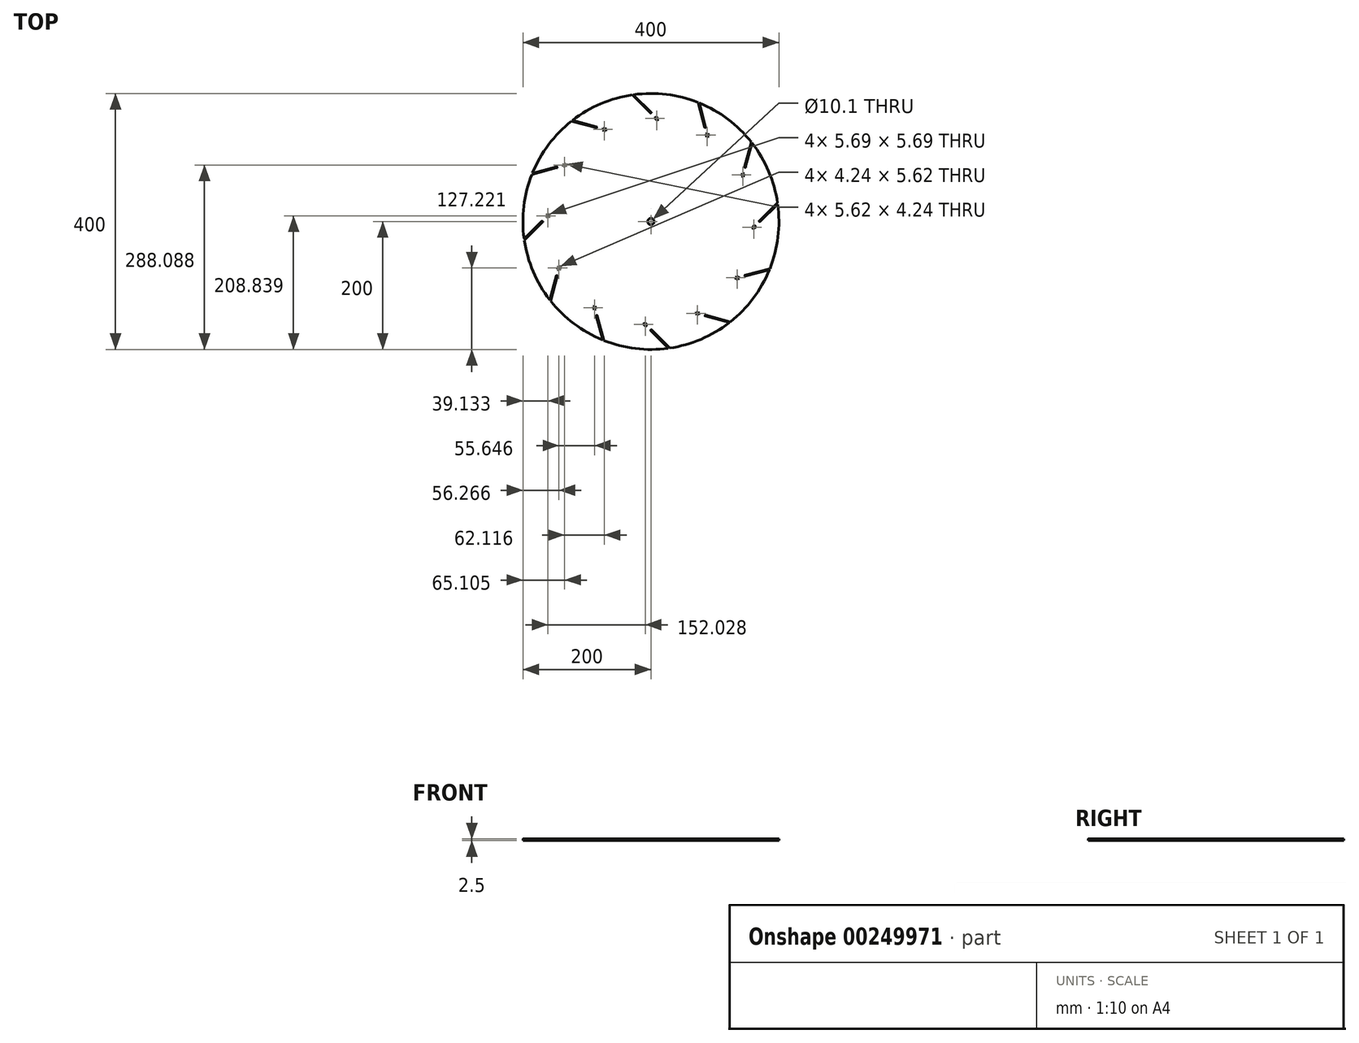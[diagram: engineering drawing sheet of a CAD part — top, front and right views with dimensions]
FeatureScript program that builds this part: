
annotation { "Feature Type Name" : "Feature", "Feature Type Description" : "" }
export const myFeature = defineFeature(function(context is Context, id is Id, definition is map)
    precondition{}
    {
        {
            var Q0;
            Q0=qCreatedBy(makeId("Top.planeOp"),FACE);
            var sketch = newSketch(context, id + "F0", { "sketchPlane" : qUnion([Q0])});
            skArc(sketch, "E0", {"start": v(-197.85, -29.24) * mm, "mid": v(-184.02, -78.33) * mm, "end": v(-158.23, -122.33) * mm});
            skLineSegment(sketch, "E1", {"start": v(28.28, 28.28) * mm, "end": v(-28.28, -28.28) * mm, "construction": true});
            skCircle(sketch, "E2", {"center": v(0, 0) * mm, "radius": 40 * mm, "construction": true});
            skLineSegment(sketch, "E3", {"start": v(40, 0) * mm, "end": v(-286.23, 0) * mm, "construction": true});
            skLineSegment(sketch, "E4", {"start": v(-28.28, -28.28) * mm, "end": v(-235.32, -28.28) * mm, "construction": true});
            skLineSegment(sketch, "E5", {"start": v(-197.99, -28.28) * mm, "end": v(-113.58, 56.13) * mm, "construction": true});
            skPoint(sketch, "E6", {"position": v(-169.7, 0) * mm});
            skCircle(sketch, "E7", {"center": v(0, 0) * mm, "radius": 169.7 * mm, "construction": true});
            skCircle(sketch, "E8", {"center": v(-169.7, 0) * mm, "radius": 0.78 * mm, "construction": true});
            skPoint(sketch, "E9", {"position": v(-197.99, -28.28) * mm});
            skLineSegment(sketch, "E10", {"start": v(-197.44, -28.83) * mm, "end": v(-198.54, -27.74) * mm, "construction": true});
            skCircle(sketch, "E11", {"center": v(-169.7, 0) * mm, "radius": 40 * mm, "construction": true});
            skLineSegment(sketch, "E12.trimOffspring", {"start": v(-170.36, 0.44) * mm, "end": v(-197.62, -26.82) * mm});
            skLineSegment(sketch, "E13.trimOffspring", {"start": v(-169.26, -0.65) * mm, "end": v(-197.85, -29.24) * mm});
            skLineSegment(sketch, "E14", {"start": v(-170.15, 0.44) * mm, "end": v(-169.26, -0.44) * mm});
            skLineSegment(sketch, "E15.MirrorCS", {"start": v(-170.25, 0.55) * mm, "end": v(-141.97, 28.83) * mm, "construction": true});
            skLineSegment(sketch, "E16.MirrorCS", {"start": v(-169.16, -0.55) * mm, "end": v(-140.87, 27.74) * mm, "construction": true});
            skLineSegment(sketch, "E17.MirrorCS", {"start": v(-140.87, 27.74) * mm, "end": v(-141.97, 28.83) * mm, "construction": true});
            skLineSegment(sketch, "E18", {"start": v(-163.71, 8.15) * mm, "end": v(-161.56, 6) * mm});
            skLineSegment(sketch, "E19", {"start": v(-160.18, 11.68) * mm, "end": v(-158.02, 9.53) * mm});
            skLineSegment(sketch, "E20.trimOffspring", {"start": v(-161.56, 6) * mm, "end": v(-158.02, 9.53) * mm});
            skLineSegment(sketch, "E21.trimOffspring", {"start": v(-163.71, 8.15) * mm, "end": v(-160.18, 11.68) * mm});
            skLineSegment(sketch, "E22.trimOffspring", {"start": v(-198.53, -27.73) * mm, "end": v(-198.54, -27.74) * mm});
            skCircle(sketch, "E23", {"center": v(0, 0) * mm, "radius": 5.05 * mm});
            skArc(sketch, "E24", {"start": v(-170.15, 0.44) * mm, "mid": v(-170.25, 0.7) * mm, "end": v(-170.36, 0.44) * mm});
            skArc(sketch, "E25.MirrorC", {"start": v(-169.26, -0.44) * mm, "mid": v(-169, -0.55) * mm, "end": v(-169.26, -0.65) * mm});
            skPoint(sketch, "E26.orphan", {"position": v(-198.12, -27.32) * mm});
            skLineSegment(sketch, "E27.trimOffspring", {"start": v(-197.62, -26.82) * mm, "end": v(-198.2, -26.82) * mm});
            skLineSegment(sketch, "E28.1.0", {"start": v(-184.56, 75.58) * mm, "end": v(-185.05, 75.87) * mm});
            skLineSegment(sketch, "E28.1.1", {"start": v(-147.31, 85.56) * mm, "end": v(-184.56, 75.58) * mm});
            skArc(sketch, "E28.1.2", {"start": v(-147.13, 85.46) * mm, "mid": v(-147.1, 85.73) * mm, "end": v(-147.31, 85.56) * mm});
            skLineSegment(sketch, "E28.1.3", {"start": v(-147.13, 85.46) * mm, "end": v(-146.8, 84.25) * mm});
            skArc(sketch, "E28.1.4", {"start": v(-146.8, 84.25) * mm, "mid": v(-146.64, 84.03) * mm, "end": v(-146.91, 84.07) * mm});
            skLineSegment(sketch, "E28.1.5", {"start": v(-146.91, 84.07) * mm, "end": v(-185.96, 73.6) * mm});
            skLineSegment(sketch, "E28.1.6", {"start": v(-137.7, 88.91) * mm, "end": v(-132.88, 90.2) * mm});
            skLineSegment(sketch, "E28.1.7", {"start": v(-132.88, 90.2) * mm, "end": v(-132.09, 87.26) * mm});
            skLineSegment(sketch, "E28.1.8", {"start": v(-136.92, 85.97) * mm, "end": v(-132.09, 87.26) * mm});
            skLineSegment(sketch, "E28.1.9", {"start": v(-137.7, 88.91) * mm, "end": v(-136.92, 85.97) * mm});
            skLineSegment(sketch, "E28.2.0", {"start": v(-122.04, 157.74) * mm, "end": v(-122.33, 158.23) * mm});
            skLineSegment(sketch, "E28.2.1", {"start": v(-84.8, 147.76) * mm, "end": v(-122.04, 157.74) * mm});
            skArc(sketch, "E28.2.2", {"start": v(-84.7, 147.57) * mm, "mid": v(-84.52, 147.8) * mm, "end": v(-84.8, 147.76) * mm});
            skLineSegment(sketch, "E28.2.3", {"start": v(-84.7, 147.57) * mm, "end": v(-85.01, 146.37) * mm});
            skArc(sketch, "E28.2.4", {"start": v(-85.01, 146.37) * mm, "mid": v(-84.98, 146.1) * mm, "end": v(-85.2, 146.26) * mm});
            skLineSegment(sketch, "E28.2.5", {"start": v(-85.2, 146.26) * mm, "end": v(-124.25, 156.72) * mm});
            skLineSegment(sketch, "E28.2.6", {"start": v(-74.8, 145.85) * mm, "end": v(-69.97, 144.56) * mm});
            skLineSegment(sketch, "E28.2.7", {"start": v(-69.97, 144.56) * mm, "end": v(-70.76, 141.61) * mm});
            skLineSegment(sketch, "E28.2.8", {"start": v(-75.59, 142.9) * mm, "end": v(-70.76, 141.61) * mm});
            skLineSegment(sketch, "E28.2.9", {"start": v(-74.8, 145.85) * mm, "end": v(-75.59, 142.9) * mm});
            skLineSegment(sketch, "E28.3.0", {"start": v(-26.82, 197.62) * mm, "end": v(-26.82, 198.2) * mm});
            skLineSegment(sketch, "E28.3.1", {"start": v(0.44, 170.36) * mm, "end": v(-26.82, 197.62) * mm});
            skArc(sketch, "E28.3.2", {"start": v(0.44, 170.15) * mm, "mid": v(0.7, 170.25) * mm, "end": v(0.44, 170.36) * mm});
            skLineSegment(sketch, "E28.3.3", {"start": v(0.44, 170.15) * mm, "end": v(-0.44, 169.26) * mm});
            skArc(sketch, "E28.3.4", {"start": v(-0.44, 169.26) * mm, "mid": v(-0.55, 169) * mm, "end": v(-0.65, 169.26) * mm});
            skLineSegment(sketch, "E28.3.5", {"start": v(-0.65, 169.26) * mm, "end": v(-29.24, 197.85) * mm});
            skLineSegment(sketch, "E28.3.6", {"start": v(8.15, 163.71) * mm, "end": v(11.68, 160.18) * mm});
            skLineSegment(sketch, "E28.3.7", {"start": v(11.68, 160.18) * mm, "end": v(9.53, 158.02) * mm});
            skLineSegment(sketch, "E28.3.8", {"start": v(6, 161.56) * mm, "end": v(9.53, 158.02) * mm});
            skLineSegment(sketch, "E28.3.9", {"start": v(8.15, 163.71) * mm, "end": v(6, 161.56) * mm});
            skLineSegment(sketch, "E28.4.0", {"start": v(75.58, 184.56) * mm, "end": v(75.87, 185.05) * mm});
            skLineSegment(sketch, "E28.4.1", {"start": v(85.56, 147.31) * mm, "end": v(75.58, 184.56) * mm});
            skArc(sketch, "E28.4.2", {"start": v(85.46, 147.13) * mm, "mid": v(85.73, 147.1) * mm, "end": v(85.56, 147.31) * mm});
            skLineSegment(sketch, "E28.4.3", {"start": v(85.46, 147.13) * mm, "end": v(84.25, 146.8) * mm});
            skArc(sketch, "E28.4.4", {"start": v(84.25, 146.8) * mm, "mid": v(84.03, 146.64) * mm, "end": v(84.07, 146.91) * mm});
            skLineSegment(sketch, "E28.4.5", {"start": v(84.07, 146.91) * mm, "end": v(73.6, 185.96) * mm});
            skLineSegment(sketch, "E28.4.6", {"start": v(88.91, 137.7) * mm, "end": v(90.2, 132.88) * mm});
            skLineSegment(sketch, "E28.4.7", {"start": v(90.2, 132.88) * mm, "end": v(87.26, 132.09) * mm});
            skLineSegment(sketch, "E28.4.8", {"start": v(85.97, 136.92) * mm, "end": v(87.26, 132.09) * mm});
            skLineSegment(sketch, "E28.4.9", {"start": v(88.91, 137.7) * mm, "end": v(85.97, 136.92) * mm});
            skLineSegment(sketch, "E28.5.0", {"start": v(157.74, 122.04) * mm, "end": v(158.23, 122.33) * mm});
            skLineSegment(sketch, "E28.5.1", {"start": v(147.76, 84.8) * mm, "end": v(157.74, 122.04) * mm});
            skArc(sketch, "E28.5.2", {"start": v(147.57, 84.7) * mm, "mid": v(147.8, 84.52) * mm, "end": v(147.76, 84.8) * mm});
            skLineSegment(sketch, "E28.5.3", {"start": v(147.57, 84.7) * mm, "end": v(146.37, 85.01) * mm});
            skArc(sketch, "E28.5.4", {"start": v(146.37, 85.01) * mm, "mid": v(146.1, 84.98) * mm, "end": v(146.26, 85.2) * mm});
            skLineSegment(sketch, "E28.5.5", {"start": v(146.26, 85.2) * mm, "end": v(156.72, 124.25) * mm});
            skLineSegment(sketch, "E28.5.6", {"start": v(145.85, 74.8) * mm, "end": v(144.56, 69.97) * mm});
            skLineSegment(sketch, "E28.5.7", {"start": v(144.56, 69.97) * mm, "end": v(141.61, 70.76) * mm});
            skLineSegment(sketch, "E28.5.8", {"start": v(142.9, 75.59) * mm, "end": v(141.61, 70.76) * mm});
            skLineSegment(sketch, "E28.5.9", {"start": v(145.85, 74.8) * mm, "end": v(142.9, 75.59) * mm});
            skLineSegment(sketch, "E28.6.0", {"start": v(197.62, 26.82) * mm, "end": v(198.2, 26.82) * mm});
            skLineSegment(sketch, "E28.6.1", {"start": v(170.36, -0.44) * mm, "end": v(197.62, 26.82) * mm});
            skArc(sketch, "E28.6.2", {"start": v(170.15, -0.44) * mm, "mid": v(170.25, -0.7) * mm, "end": v(170.36, -0.44) * mm});
            skLineSegment(sketch, "E28.6.3", {"start": v(170.15, -0.44) * mm, "end": v(169.26, 0.44) * mm});
            skArc(sketch, "E28.6.4", {"start": v(169.26, 0.44) * mm, "mid": v(169, 0.55) * mm, "end": v(169.26, 0.65) * mm});
            skLineSegment(sketch, "E28.6.5", {"start": v(169.26, 0.65) * mm, "end": v(197.85, 29.24) * mm});
            skLineSegment(sketch, "E28.6.6", {"start": v(163.71, -8.15) * mm, "end": v(160.18, -11.68) * mm});
            skLineSegment(sketch, "E28.6.7", {"start": v(160.18, -11.68) * mm, "end": v(158.02, -9.53) * mm});
            skLineSegment(sketch, "E28.6.8", {"start": v(161.56, -6) * mm, "end": v(158.02, -9.53) * mm});
            skLineSegment(sketch, "E28.6.9", {"start": v(163.71, -8.15) * mm, "end": v(161.56, -6) * mm});
            skLineSegment(sketch, "E28.7.0", {"start": v(184.56, -75.58) * mm, "end": v(185.05, -75.87) * mm});
            skLineSegment(sketch, "E28.7.1", {"start": v(147.31, -85.56) * mm, "end": v(184.56, -75.58) * mm});
            skArc(sketch, "E28.7.2", {"start": v(147.13, -85.46) * mm, "mid": v(147.1, -85.73) * mm, "end": v(147.31, -85.56) * mm});
            skLineSegment(sketch, "E28.7.3", {"start": v(147.13, -85.46) * mm, "end": v(146.8, -84.25) * mm});
            skArc(sketch, "E28.7.4", {"start": v(146.8, -84.25) * mm, "mid": v(146.64, -84.03) * mm, "end": v(146.91, -84.07) * mm});
            skLineSegment(sketch, "E28.7.5", {"start": v(146.91, -84.07) * mm, "end": v(185.96, -73.6) * mm});
            skLineSegment(sketch, "E28.7.6", {"start": v(137.7, -88.91) * mm, "end": v(132.88, -90.2) * mm});
            skLineSegment(sketch, "E28.7.7", {"start": v(132.88, -90.2) * mm, "end": v(132.09, -87.26) * mm});
            skLineSegment(sketch, "E28.7.8", {"start": v(136.92, -85.97) * mm, "end": v(132.09, -87.26) * mm});
            skLineSegment(sketch, "E28.7.9", {"start": v(137.7, -88.91) * mm, "end": v(136.92, -85.97) * mm});
            skLineSegment(sketch, "E28.8.0", {"start": v(122.04, -157.74) * mm, "end": v(122.33, -158.23) * mm});
            skLineSegment(sketch, "E28.8.1", {"start": v(84.8, -147.76) * mm, "end": v(122.04, -157.74) * mm});
            skArc(sketch, "E28.8.2", {"start": v(84.7, -147.57) * mm, "mid": v(84.52, -147.8) * mm, "end": v(84.8, -147.76) * mm});
            skLineSegment(sketch, "E28.8.3", {"start": v(84.7, -147.57) * mm, "end": v(85.01, -146.37) * mm});
            skArc(sketch, "E28.8.4", {"start": v(85.01, -146.37) * mm, "mid": v(84.98, -146.1) * mm, "end": v(85.2, -146.26) * mm});
            skLineSegment(sketch, "E28.8.5", {"start": v(85.2, -146.26) * mm, "end": v(124.25, -156.72) * mm});
            skLineSegment(sketch, "E28.8.6", {"start": v(74.8, -145.85) * mm, "end": v(69.97, -144.56) * mm});
            skLineSegment(sketch, "E28.8.7", {"start": v(69.97, -144.56) * mm, "end": v(70.76, -141.61) * mm});
            skLineSegment(sketch, "E28.8.8", {"start": v(75.59, -142.9) * mm, "end": v(70.76, -141.61) * mm});
            skLineSegment(sketch, "E28.8.9", {"start": v(74.8, -145.85) * mm, "end": v(75.59, -142.9) * mm});
            skLineSegment(sketch, "E28.9.0", {"start": v(26.82, -197.62) * mm, "end": v(26.82, -198.2) * mm});
            skLineSegment(sketch, "E28.9.1", {"start": v(-0.44, -170.36) * mm, "end": v(26.82, -197.62) * mm});
            skArc(sketch, "E28.9.2", {"start": v(-0.44, -170.15) * mm, "mid": v(-0.7, -170.25) * mm, "end": v(-0.44, -170.36) * mm});
            skLineSegment(sketch, "E28.9.3", {"start": v(-0.44, -170.15) * mm, "end": v(0.44, -169.26) * mm});
            skArc(sketch, "E28.9.4", {"start": v(0.44, -169.26) * mm, "mid": v(0.55, -169) * mm, "end": v(0.65, -169.26) * mm});
            skLineSegment(sketch, "E28.9.5", {"start": v(0.65, -169.26) * mm, "end": v(29.24, -197.85) * mm});
            skLineSegment(sketch, "E28.9.6", {"start": v(-8.15, -163.71) * mm, "end": v(-11.68, -160.18) * mm});
            skLineSegment(sketch, "E28.9.7", {"start": v(-11.68, -160.18) * mm, "end": v(-9.53, -158.02) * mm});
            skLineSegment(sketch, "E28.9.8", {"start": v(-6, -161.56) * mm, "end": v(-9.53, -158.02) * mm});
            skLineSegment(sketch, "E28.9.9", {"start": v(-8.15, -163.71) * mm, "end": v(-6, -161.56) * mm});
            skLineSegment(sketch, "E28.10.0", {"start": v(-75.58, -184.56) * mm, "end": v(-75.87, -185.05) * mm});
            skLineSegment(sketch, "E28.10.1", {"start": v(-85.56, -147.31) * mm, "end": v(-75.58, -184.56) * mm});
            skArc(sketch, "E28.10.2", {"start": v(-85.46, -147.13) * mm, "mid": v(-85.73, -147.1) * mm, "end": v(-85.56, -147.31) * mm});
            skLineSegment(sketch, "E28.10.3", {"start": v(-85.46, -147.13) * mm, "end": v(-84.25, -146.8) * mm});
            skArc(sketch, "E28.10.4", {"start": v(-84.25, -146.8) * mm, "mid": v(-84.03, -146.64) * mm, "end": v(-84.07, -146.91) * mm});
            skLineSegment(sketch, "E28.10.5", {"start": v(-84.07, -146.91) * mm, "end": v(-73.6, -185.96) * mm});
            skLineSegment(sketch, "E28.10.6", {"start": v(-88.91, -137.7) * mm, "end": v(-90.2, -132.88) * mm});
            skLineSegment(sketch, "E28.10.7", {"start": v(-90.2, -132.88) * mm, "end": v(-87.26, -132.09) * mm});
            skLineSegment(sketch, "E28.10.8", {"start": v(-85.97, -136.92) * mm, "end": v(-87.26, -132.09) * mm});
            skLineSegment(sketch, "E28.10.9", {"start": v(-88.91, -137.7) * mm, "end": v(-85.97, -136.92) * mm});
            skLineSegment(sketch, "E28.11.0", {"start": v(-157.74, -122.04) * mm, "end": v(-158.23, -122.33) * mm});
            skLineSegment(sketch, "E28.11.1", {"start": v(-147.76, -84.8) * mm, "end": v(-157.74, -122.04) * mm});
            skArc(sketch, "E28.11.2", {"start": v(-147.57, -84.7) * mm, "mid": v(-147.8, -84.52) * mm, "end": v(-147.76, -84.8) * mm});
            skLineSegment(sketch, "E28.11.3", {"start": v(-147.57, -84.7) * mm, "end": v(-146.37, -85.01) * mm});
            skArc(sketch, "E28.11.4", {"start": v(-146.37, -85.01) * mm, "mid": v(-146.1, -84.98) * mm, "end": v(-146.26, -85.2) * mm});
            skLineSegment(sketch, "E28.11.5", {"start": v(-146.26, -85.2) * mm, "end": v(-156.72, -124.25) * mm});
            skLineSegment(sketch, "E28.11.6", {"start": v(-145.85, -74.8) * mm, "end": v(-144.56, -69.97) * mm});
            skLineSegment(sketch, "E28.11.7", {"start": v(-144.56, -69.97) * mm, "end": v(-141.61, -70.76) * mm});
            skLineSegment(sketch, "E28.11.8", {"start": v(-142.9, -75.59) * mm, "end": v(-141.61, -70.76) * mm});
            skLineSegment(sketch, "E28.11.9", {"start": v(-145.85, -74.8) * mm, "end": v(-142.9, -75.59) * mm});
            skLineSegment(sketch, "E28.anchor1", {"start": v(0, 0) * mm, "end": v(-198.2, -26.82) * mm, "construction": true});
            skLineSegment(sketch, "E28.anchor2", {"start": v(0, 0) * mm, "end": v(-158.23, -122.33) * mm, "construction": true});
            skArc(sketch, "E29.trimOffspring", {"start": v(-185.96, 73.6) * mm, "mid": v(-198.53, 24.18) * mm, "end": v(-198.2, -26.82) * mm});
            skArc(sketch, "E30.trimOffspring", {"start": v(-124.25, 156.72) * mm, "mid": v(-159.85, 120.2) * mm, "end": v(-185.05, 75.87) * mm});
            skArc(sketch, "E31.trimOffspring", {"start": v(-29.24, 197.85) * mm, "mid": v(-78.33, 184.02) * mm, "end": v(-122.33, 158.23) * mm});
            skArc(sketch, "E32.trimOffspring", {"start": v(73.6, 185.96) * mm, "mid": v(24.18, 198.53) * mm, "end": v(-26.82, 198.2) * mm});
            skArc(sketch, "E33.trimOffspring", {"start": v(156.72, 124.25) * mm, "mid": v(120.2, 159.85) * mm, "end": v(75.87, 185.05) * mm});
            skArc(sketch, "E34.trimOffspring", {"start": v(197.85, 29.24) * mm, "mid": v(184.02, 78.33) * mm, "end": v(158.23, 122.33) * mm});
            skArc(sketch, "E35.trimOffspring", {"start": v(185.96, -73.6) * mm, "mid": v(198.53, -24.18) * mm, "end": v(198.2, 26.82) * mm});
            skArc(sketch, "E36.trimOffspring", {"start": v(124.25, -156.72) * mm, "mid": v(159.85, -120.2) * mm, "end": v(185.05, -75.87) * mm});
            skArc(sketch, "E37.trimOffspring", {"start": v(29.24, -197.85) * mm, "mid": v(78.33, -184.02) * mm, "end": v(122.33, -158.23) * mm});
            skArc(sketch, "E38.trimOffspring", {"start": v(-73.6, -185.96) * mm, "mid": v(-24.18, -198.53) * mm, "end": v(26.82, -198.2) * mm});
            skArc(sketch, "E39.trimOffspring", {"start": v(-156.72, -124.25) * mm, "mid": v(-120.2, -159.85) * mm, "end": v(-75.87, -185.05) * mm});
            skSolve(sketch);
        }
        {
            var Q0;
            Q0 = qSketchRegion(id + "F0", true);
            extrude(context, id + "F1", {"entities" : qUnion([Q0]), "depth" : 1.25 * mm, "hasSecondDirection" : true, "secondDirectionOppositeDirection" : true, "secondDirectionDepth" : 1.25 * mm});
        }
    });
